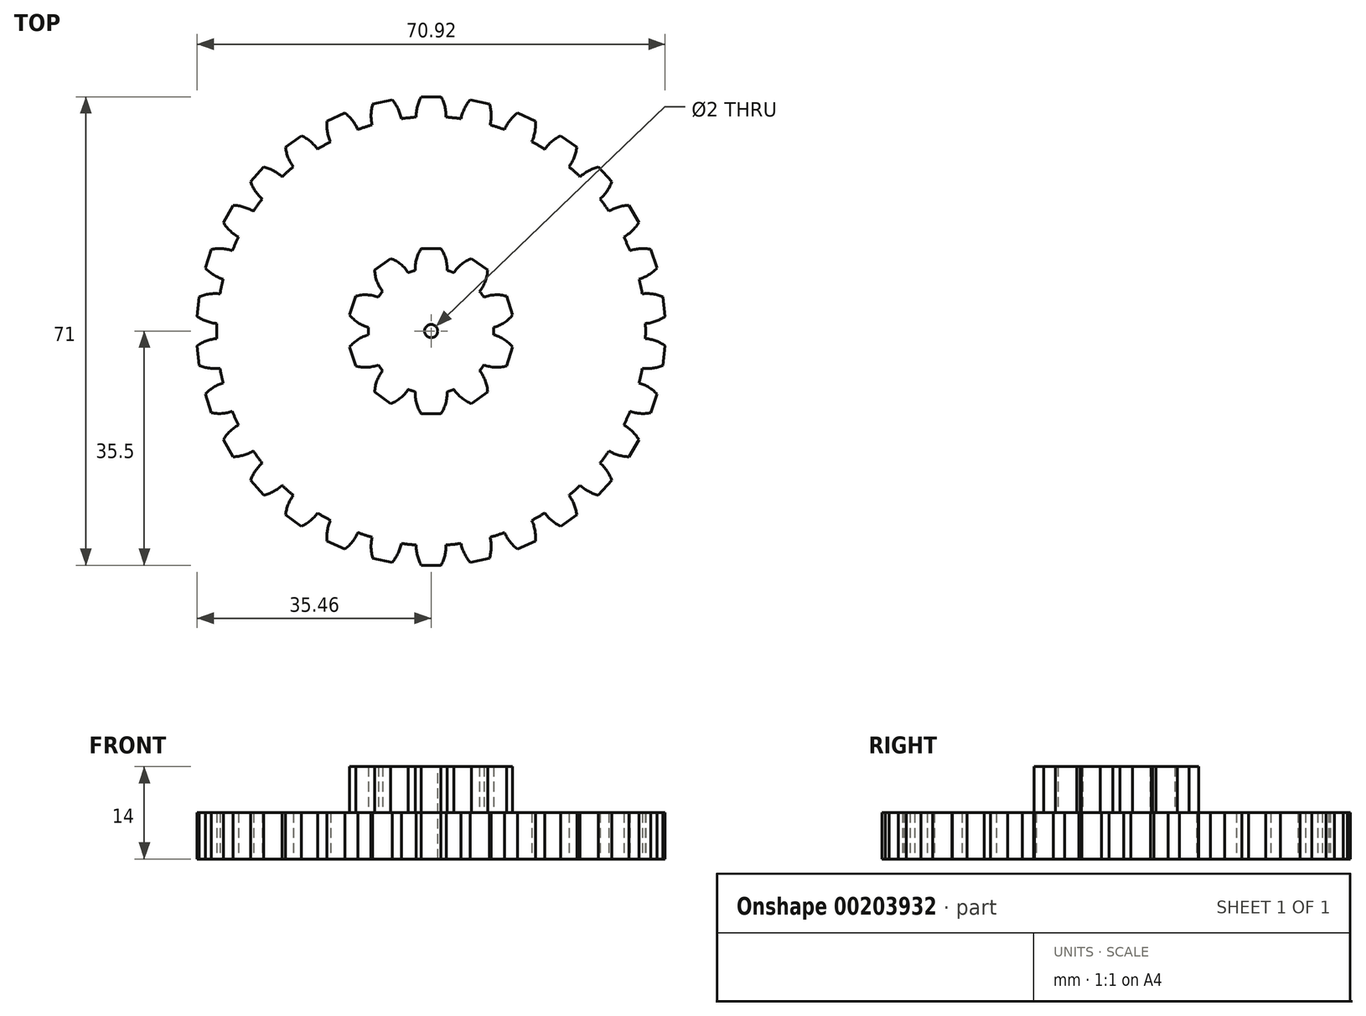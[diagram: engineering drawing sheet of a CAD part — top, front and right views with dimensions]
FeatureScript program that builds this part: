
annotation { "Feature Type Name" : "Feature", "Feature Type Description" : "" }
export const myFeature = defineFeature(function(context is Context, id is Id, definition is map)
    precondition{}
    {
        {
            var Q0;
            Q0=qCreatedBy(makeId("Top.planeOp"),FACE);
            var sketch = newSketch(context, id + "F0", { "sketchPlane" : qUnion([Q0])});
            skCircle(sketch, "E0", {"center": v(0, 0) * mm, "radius": 32.5 * mm});
            skLineSegment(sketch, "E1", {"start": v(0, 0) * mm, "end": v(0, 32.5) * mm, "construction": true});
            skLineSegment(sketch, "E2", {"start": v(0, 35.5) * mm, "end": v(-1.5, 35.5) * mm});
            skArc(sketch, "E3", {"start": v(-1.5, 35.5) * mm, "mid": v(-2.08, 34) * mm, "end": v(-2.26, 32.42) * mm});
            skLineSegment(sketch, "E4.MirrorCS", {"start": v(0, 35.5) * mm, "end": v(1.5, 35.5) * mm});
            skArc(sketch, "E5.MirrorCS", {"start": v(1.5, 35.5) * mm, "mid": v(2.08, 34) * mm, "end": v(2.26, 32.42) * mm});
            skArc(sketch, "E6.1.0", {"start": v(-8.85, 34.41) * mm, "mid": v(-9.1, 32.83) * mm, "end": v(-8.96, 31.24) * mm});
            skLineSegment(sketch, "E6.1.1", {"start": v(-7.38, 34.72) * mm, "end": v(-8.85, 34.41) * mm});
            skLineSegment(sketch, "E6.1.2", {"start": v(-7.38, 34.72) * mm, "end": v(-5.91, 35.04) * mm});
            skArc(sketch, "E6.1.3", {"start": v(-5.91, 35.04) * mm, "mid": v(-5.04, 33.7) * mm, "end": v(-4.53, 32.18) * mm});
            skArc(sketch, "E6.2.0", {"start": v(-15.8, 31.82) * mm, "mid": v(-15.73, 30.22) * mm, "end": v(-15.26, 28.7) * mm});
            skLineSegment(sketch, "E6.2.1", {"start": v(-14.44, 32.43) * mm, "end": v(-15.8, 31.82) * mm});
            skLineSegment(sketch, "E6.2.2", {"start": v(-14.44, 32.43) * mm, "end": v(-13.07, 33.04) * mm});
            skArc(sketch, "E6.2.3", {"start": v(-13.07, 33.04) * mm, "mid": v(-11.93, 31.92) * mm, "end": v(-11.12, 30.54) * mm});
            skArc(sketch, "E6.3.0", {"start": v(-22.08, 27.84) * mm, "mid": v(-21.67, 26.3) * mm, "end": v(-20.89, 24.9) * mm});
            skLineSegment(sketch, "E6.3.1", {"start": v(-20.87, 28.72) * mm, "end": v(-22.08, 27.84) * mm});
            skLineSegment(sketch, "E6.3.2", {"start": v(-20.87, 28.72) * mm, "end": v(-19.65, 29.6) * mm});
            skArc(sketch, "E6.3.3", {"start": v(-19.65, 29.6) * mm, "mid": v(-18.3, 28.74) * mm, "end": v(-17.22, 27.56) * mm});
            skArc(sketch, "E6.4.0", {"start": v(-27.39, 22.64) * mm, "mid": v(-26.67, 21.21) * mm, "end": v(-25.6, 20.01) * mm});
            skLineSegment(sketch, "E6.4.1", {"start": v(-26.38, 23.75) * mm, "end": v(-27.39, 22.64) * mm});
            skLineSegment(sketch, "E6.4.2", {"start": v(-26.38, 23.75) * mm, "end": v(-25.38, 24.87) * mm});
            skArc(sketch, "E6.4.3", {"start": v(-25.38, 24.87) * mm, "mid": v(-23.88, 24.3) * mm, "end": v(-22.58, 23.38) * mm});
            skArc(sketch, "E6.5.0", {"start": v(-31.5, 16.45) * mm, "mid": v(-30.5, 15.2) * mm, "end": v(-29.2, 14.25) * mm});
            skLineSegment(sketch, "E6.5.1", {"start": v(-30.74, 17.75) * mm, "end": v(-31.5, 16.45) * mm});
            skLineSegment(sketch, "E6.5.2", {"start": v(-30.74, 17.75) * mm, "end": v(-30, 19.05) * mm});
            skArc(sketch, "E6.5.3", {"start": v(-30, 19.05) * mm, "mid": v(-28.41, 18.8) * mm, "end": v(-26.95, 18.17) * mm});
            skArc(sketch, "E6.6.0", {"start": v(-34.23, 9.54) * mm, "mid": v(-32.99, 8.53) * mm, "end": v(-31.53, 7.86) * mm});
            skLineSegment(sketch, "E6.6.1", {"start": v(-33.76, 10.97) * mm, "end": v(-34.23, 9.54) * mm});
            skLineSegment(sketch, "E6.6.2", {"start": v(-33.76, 10.97) * mm, "end": v(-33.3, 12.4) * mm});
            skArc(sketch, "E6.6.3", {"start": v(-33.3, 12.4) * mm, "mid": v(-31.7, 12.49) * mm, "end": v(-30.13, 12.17) * mm});
            skArc(sketch, "E6.7.0", {"start": v(-35.46, 2.22) * mm, "mid": v(-34.04, 1.49) * mm, "end": v(-32.48, 1.14) * mm});
            skLineSegment(sketch, "E6.7.1", {"start": v(-35.3, 3.71) * mm, "end": v(-35.46, 2.22) * mm});
            skLineSegment(sketch, "E6.7.2", {"start": v(-35.3, 3.71) * mm, "end": v(-35.15, 5.2) * mm});
            skArc(sketch, "E6.7.3", {"start": v(-35.15, 5.2) * mm, "mid": v(-33.6, 5.62) * mm, "end": v(-32, 5.64) * mm});
            skArc(sketch, "E6.8.0", {"start": v(-35.15, -5.2) * mm, "mid": v(-33.6, -5.62) * mm, "end": v(-32, -5.64) * mm});
            skLineSegment(sketch, "E6.8.1", {"start": v(-35.3, -3.71) * mm, "end": v(-35.15, -5.2) * mm});
            skLineSegment(sketch, "E6.8.2", {"start": v(-35.3, -3.71) * mm, "end": v(-35.46, -2.22) * mm});
            skArc(sketch, "E6.8.3", {"start": v(-35.46, -2.22) * mm, "mid": v(-34.04, -1.49) * mm, "end": v(-32.48, -1.14) * mm});
            skArc(sketch, "E6.9.0", {"start": v(-33.3, -12.4) * mm, "mid": v(-31.7, -12.49) * mm, "end": v(-30.13, -12.17) * mm});
            skLineSegment(sketch, "E6.9.1", {"start": v(-33.76, -10.97) * mm, "end": v(-33.3, -12.4) * mm});
            skLineSegment(sketch, "E6.9.2", {"start": v(-33.76, -10.97) * mm, "end": v(-34.23, -9.54) * mm});
            skArc(sketch, "E6.9.3", {"start": v(-34.23, -9.54) * mm, "mid": v(-32.99, -8.53) * mm, "end": v(-31.53, -7.86) * mm});
            skArc(sketch, "E6.10.0", {"start": v(-30, -19.05) * mm, "mid": v(-28.41, -18.8) * mm, "end": v(-26.95, -18.17) * mm});
            skLineSegment(sketch, "E6.10.1", {"start": v(-30.74, -17.75) * mm, "end": v(-30, -19.05) * mm});
            skLineSegment(sketch, "E6.10.2", {"start": v(-30.74, -17.75) * mm, "end": v(-31.5, -16.45) * mm});
            skArc(sketch, "E6.10.3", {"start": v(-31.5, -16.45) * mm, "mid": v(-30.5, -15.2) * mm, "end": v(-29.2, -14.25) * mm});
            skArc(sketch, "E6.11.0", {"start": v(-25.38, -24.87) * mm, "mid": v(-23.88, -24.3) * mm, "end": v(-22.58, -23.38) * mm});
            skLineSegment(sketch, "E6.11.1", {"start": v(-26.38, -23.75) * mm, "end": v(-25.38, -24.87) * mm});
            skLineSegment(sketch, "E6.11.2", {"start": v(-26.38, -23.75) * mm, "end": v(-27.39, -22.64) * mm});
            skArc(sketch, "E6.11.3", {"start": v(-27.39, -22.64) * mm, "mid": v(-26.67, -21.21) * mm, "end": v(-25.6, -20.01) * mm});
            skArc(sketch, "E6.12.0", {"start": v(-19.65, -29.6) * mm, "mid": v(-18.3, -28.74) * mm, "end": v(-17.22, -27.56) * mm});
            skLineSegment(sketch, "E6.12.1", {"start": v(-20.87, -28.72) * mm, "end": v(-19.65, -29.6) * mm});
            skLineSegment(sketch, "E6.12.2", {"start": v(-20.87, -28.72) * mm, "end": v(-22.08, -27.84) * mm});
            skArc(sketch, "E6.12.3", {"start": v(-22.08, -27.84) * mm, "mid": v(-21.67, -26.3) * mm, "end": v(-20.89, -24.9) * mm});
            skArc(sketch, "E6.13.0", {"start": v(-13.07, -33.04) * mm, "mid": v(-11.93, -31.92) * mm, "end": v(-11.12, -30.54) * mm});
            skLineSegment(sketch, "E6.13.1", {"start": v(-14.44, -32.43) * mm, "end": v(-13.07, -33.04) * mm});
            skLineSegment(sketch, "E6.13.2", {"start": v(-14.44, -32.43) * mm, "end": v(-15.8, -31.82) * mm});
            skArc(sketch, "E6.13.3", {"start": v(-15.8, -31.82) * mm, "mid": v(-15.73, -30.22) * mm, "end": v(-15.26, -28.7) * mm});
            skArc(sketch, "E6.14.0", {"start": v(-5.91, -35.04) * mm, "mid": v(-5.04, -33.7) * mm, "end": v(-4.53, -32.18) * mm});
            skLineSegment(sketch, "E6.14.1", {"start": v(-7.38, -34.72) * mm, "end": v(-5.91, -35.04) * mm});
            skLineSegment(sketch, "E6.14.2", {"start": v(-7.38, -34.72) * mm, "end": v(-8.85, -34.41) * mm});
            skArc(sketch, "E6.14.3", {"start": v(-8.85, -34.41) * mm, "mid": v(-9.1, -32.83) * mm, "end": v(-8.96, -31.24) * mm});
            skArc(sketch, "E6.15.0", {"start": v(1.5, -35.5) * mm, "mid": v(2.08, -34) * mm, "end": v(2.26, -32.42) * mm});
            skLineSegment(sketch, "E6.15.1", {"start": v(0, -35.5) * mm, "end": v(1.5, -35.5) * mm});
            skLineSegment(sketch, "E6.15.2", {"start": v(0, -35.5) * mm, "end": v(-1.5, -35.5) * mm});
            skArc(sketch, "E6.15.3", {"start": v(-1.5, -35.5) * mm, "mid": v(-2.08, -34) * mm, "end": v(-2.26, -32.42) * mm});
            skArc(sketch, "E6.16.0", {"start": v(8.85, -34.41) * mm, "mid": v(9.1, -32.83) * mm, "end": v(8.96, -31.24) * mm});
            skLineSegment(sketch, "E6.16.1", {"start": v(7.38, -34.72) * mm, "end": v(8.85, -34.41) * mm});
            skLineSegment(sketch, "E6.16.2", {"start": v(7.38, -34.72) * mm, "end": v(5.91, -35.04) * mm});
            skArc(sketch, "E6.16.3", {"start": v(5.91, -35.04) * mm, "mid": v(5.04, -33.7) * mm, "end": v(4.53, -32.18) * mm});
            skArc(sketch, "E6.17.0", {"start": v(15.8, -31.82) * mm, "mid": v(15.73, -30.22) * mm, "end": v(15.26, -28.7) * mm});
            skLineSegment(sketch, "E6.17.1", {"start": v(14.44, -32.43) * mm, "end": v(15.8, -31.82) * mm});
            skLineSegment(sketch, "E6.17.2", {"start": v(14.44, -32.43) * mm, "end": v(13.07, -33.04) * mm});
            skArc(sketch, "E6.17.3", {"start": v(13.07, -33.04) * mm, "mid": v(11.93, -31.92) * mm, "end": v(11.12, -30.54) * mm});
            skArc(sketch, "E6.18.0", {"start": v(22.08, -27.84) * mm, "mid": v(21.67, -26.3) * mm, "end": v(20.89, -24.9) * mm});
            skLineSegment(sketch, "E6.18.1", {"start": v(20.87, -28.72) * mm, "end": v(22.08, -27.84) * mm});
            skLineSegment(sketch, "E6.18.2", {"start": v(20.87, -28.72) * mm, "end": v(19.65, -29.6) * mm});
            skArc(sketch, "E6.18.3", {"start": v(19.65, -29.6) * mm, "mid": v(18.3, -28.74) * mm, "end": v(17.22, -27.56) * mm});
            skArc(sketch, "E6.19.0", {"start": v(27.39, -22.64) * mm, "mid": v(26.67, -21.21) * mm, "end": v(25.6, -20.01) * mm});
            skLineSegment(sketch, "E6.19.1", {"start": v(26.38, -23.75) * mm, "end": v(27.39, -22.64) * mm});
            skLineSegment(sketch, "E6.19.2", {"start": v(26.38, -23.75) * mm, "end": v(25.38, -24.87) * mm});
            skArc(sketch, "E6.19.3", {"start": v(25.38, -24.87) * mm, "mid": v(23.88, -24.3) * mm, "end": v(22.58, -23.38) * mm});
            skArc(sketch, "E6.20.0", {"start": v(31.5, -16.45) * mm, "mid": v(30.5, -15.2) * mm, "end": v(29.2, -14.25) * mm});
            skLineSegment(sketch, "E6.20.1", {"start": v(30.74, -17.75) * mm, "end": v(31.5, -16.45) * mm});
            skLineSegment(sketch, "E6.20.2", {"start": v(30.74, -17.75) * mm, "end": v(30, -19.05) * mm});
            skArc(sketch, "E6.20.3", {"start": v(30, -19.05) * mm, "mid": v(28.41, -18.8) * mm, "end": v(26.95, -18.17) * mm});
            skArc(sketch, "E6.21.0", {"start": v(34.23, -9.54) * mm, "mid": v(32.99, -8.53) * mm, "end": v(31.53, -7.86) * mm});
            skLineSegment(sketch, "E6.21.1", {"start": v(33.76, -10.97) * mm, "end": v(34.23, -9.54) * mm});
            skLineSegment(sketch, "E6.21.2", {"start": v(33.76, -10.97) * mm, "end": v(33.3, -12.4) * mm});
            skArc(sketch, "E6.21.3", {"start": v(33.3, -12.4) * mm, "mid": v(31.7, -12.49) * mm, "end": v(30.13, -12.17) * mm});
            skArc(sketch, "E6.22.0", {"start": v(35.46, -2.22) * mm, "mid": v(34.04, -1.49) * mm, "end": v(32.48, -1.14) * mm});
            skLineSegment(sketch, "E6.22.1", {"start": v(35.3, -3.71) * mm, "end": v(35.46, -2.22) * mm});
            skLineSegment(sketch, "E6.22.2", {"start": v(35.3, -3.71) * mm, "end": v(35.15, -5.2) * mm});
            skArc(sketch, "E6.22.3", {"start": v(35.15, -5.2) * mm, "mid": v(33.6, -5.62) * mm, "end": v(32, -5.64) * mm});
            skArc(sketch, "E6.23.0", {"start": v(35.15, 5.2) * mm, "mid": v(33.6, 5.62) * mm, "end": v(32, 5.64) * mm});
            skLineSegment(sketch, "E6.23.1", {"start": v(35.3, 3.71) * mm, "end": v(35.15, 5.2) * mm});
            skLineSegment(sketch, "E6.23.2", {"start": v(35.3, 3.71) * mm, "end": v(35.46, 2.22) * mm});
            skArc(sketch, "E6.23.3", {"start": v(35.46, 2.22) * mm, "mid": v(34.04, 1.49) * mm, "end": v(32.48, 1.14) * mm});
            skArc(sketch, "E6.24.0", {"start": v(33.3, 12.4) * mm, "mid": v(31.7, 12.49) * mm, "end": v(30.13, 12.17) * mm});
            skLineSegment(sketch, "E6.24.1", {"start": v(33.76, 10.97) * mm, "end": v(33.3, 12.4) * mm});
            skLineSegment(sketch, "E6.24.2", {"start": v(33.76, 10.97) * mm, "end": v(34.23, 9.54) * mm});
            skArc(sketch, "E6.24.3", {"start": v(34.23, 9.54) * mm, "mid": v(32.99, 8.53) * mm, "end": v(31.53, 7.86) * mm});
            skArc(sketch, "E6.25.0", {"start": v(30, 19.05) * mm, "mid": v(28.41, 18.8) * mm, "end": v(26.95, 18.17) * mm});
            skLineSegment(sketch, "E6.25.1", {"start": v(30.74, 17.75) * mm, "end": v(30, 19.05) * mm});
            skLineSegment(sketch, "E6.25.2", {"start": v(30.74, 17.75) * mm, "end": v(31.5, 16.45) * mm});
            skArc(sketch, "E6.25.3", {"start": v(31.5, 16.45) * mm, "mid": v(30.5, 15.2) * mm, "end": v(29.2, 14.25) * mm});
            skArc(sketch, "E6.26.0", {"start": v(25.38, 24.87) * mm, "mid": v(23.88, 24.3) * mm, "end": v(22.58, 23.38) * mm});
            skLineSegment(sketch, "E6.26.1", {"start": v(26.38, 23.75) * mm, "end": v(25.38, 24.87) * mm});
            skLineSegment(sketch, "E6.26.2", {"start": v(26.38, 23.75) * mm, "end": v(27.39, 22.64) * mm});
            skArc(sketch, "E6.26.3", {"start": v(27.39, 22.64) * mm, "mid": v(26.67, 21.21) * mm, "end": v(25.6, 20.01) * mm});
            skArc(sketch, "E6.27.0", {"start": v(19.65, 29.6) * mm, "mid": v(18.3, 28.74) * mm, "end": v(17.22, 27.56) * mm});
            skLineSegment(sketch, "E6.27.1", {"start": v(20.87, 28.72) * mm, "end": v(19.65, 29.6) * mm});
            skLineSegment(sketch, "E6.27.2", {"start": v(20.87, 28.72) * mm, "end": v(22.08, 27.84) * mm});
            skArc(sketch, "E6.27.3", {"start": v(22.08, 27.84) * mm, "mid": v(21.67, 26.3) * mm, "end": v(20.89, 24.9) * mm});
            skArc(sketch, "E6.28.0", {"start": v(13.07, 33.04) * mm, "mid": v(11.93, 31.92) * mm, "end": v(11.12, 30.54) * mm});
            skLineSegment(sketch, "E6.28.1", {"start": v(14.44, 32.43) * mm, "end": v(13.07, 33.04) * mm});
            skLineSegment(sketch, "E6.28.2", {"start": v(14.44, 32.43) * mm, "end": v(15.8, 31.82) * mm});
            skArc(sketch, "E6.28.3", {"start": v(15.8, 31.82) * mm, "mid": v(15.73, 30.22) * mm, "end": v(15.26, 28.7) * mm});
            skArc(sketch, "E6.29.0", {"start": v(5.91, 35.04) * mm, "mid": v(5.04, 33.7) * mm, "end": v(4.53, 32.18) * mm});
            skLineSegment(sketch, "E6.29.1", {"start": v(7.38, 34.72) * mm, "end": v(5.91, 35.04) * mm});
            skLineSegment(sketch, "E6.29.2", {"start": v(7.38, 34.72) * mm, "end": v(8.85, 34.41) * mm});
            skArc(sketch, "E6.29.3", {"start": v(8.85, 34.41) * mm, "mid": v(9.1, 32.83) * mm, "end": v(8.96, 31.24) * mm});
            skSolve(sketch);
        }
        {
            var Q0;
            Q0=qSketchRegion(id+"F0",true);
            extrude(context, id + "F1", {"entities" : qUnion([Q0]), "depth" : 7 * mm});
        }
        {
            var Q0;
            Q0=makeQuery(id+"F1.opExtrude","CAP_FACE",FACE,{"disambiguationData":[OSD([sQuery(id+"F0.wireOp",EDGE,"E0"),sQuery(id+"F0.wireOp",EDGE,"E2"),sQuery(id+"F0.wireOp",EDGE,"E3"),sQuery(id+"F0.wireOp",EDGE,"E4.MirrorCS"),sQuery(id+"F0.wireOp",EDGE,"E5.MirrorCS"),sQuery(id+"F0.wireOp",EDGE,"E6.1.0"),sQuery(id+"F0.wireOp",EDGE,"E6.1.1"),sQuery(id+"F0.wireOp",EDGE,"E6.1.2"),sQuery(id+"F0.wireOp",EDGE,"E6.1.3"),sQuery(id+"F0.wireOp",EDGE,"E6.2.0"),sQuery(id+"F0.wireOp",EDGE,"E6.2.1"),sQuery(id+"F0.wireOp",EDGE,"E6.2.2"),sQuery(id+"F0.wireOp",EDGE,"E6.2.3"),sQuery(id+"F0.wireOp",EDGE,"E6.3.0"),sQuery(id+"F0.wireOp",EDGE,"E6.3.1"),sQuery(id+"F0.wireOp",EDGE,"E6.3.2"),sQuery(id+"F0.wireOp",EDGE,"E6.3.3"),sQuery(id+"F0.wireOp",EDGE,"E6.4.0"),sQuery(id+"F0.wireOp",EDGE,"E6.4.1"),sQuery(id+"F0.wireOp",EDGE,"E6.4.2"),sQuery(id+"F0.wireOp",EDGE,"E6.4.3"),sQuery(id+"F0.wireOp",EDGE,"E6.5.0"),sQuery(id+"F0.wireOp",EDGE,"E6.5.1"),sQuery(id+"F0.wireOp",EDGE,"E6.5.2"),sQuery(id+"F0.wireOp",EDGE,"E6.5.3"),sQuery(id+"F0.wireOp",EDGE,"E6.6.0"),sQuery(id+"F0.wireOp",EDGE,"E6.6.1"),sQuery(id+"F0.wireOp",EDGE,"E6.6.2"),sQuery(id+"F0.wireOp",EDGE,"E6.6.3"),sQuery(id+"F0.wireOp",EDGE,"E6.7.0"),sQuery(id+"F0.wireOp",EDGE,"E6.7.1"),sQuery(id+"F0.wireOp",EDGE,"E6.7.2"),sQuery(id+"F0.wireOp",EDGE,"E6.7.3"),sQuery(id+"F0.wireOp",EDGE,"E6.8.0"),sQuery(id+"F0.wireOp",EDGE,"E6.8.1"),sQuery(id+"F0.wireOp",EDGE,"E6.8.2"),sQuery(id+"F0.wireOp",EDGE,"E6.8.3"),sQuery(id+"F0.wireOp",EDGE,"E6.9.0"),sQuery(id+"F0.wireOp",EDGE,"E6.9.1"),sQuery(id+"F0.wireOp",EDGE,"E6.9.2"),sQuery(id+"F0.wireOp",EDGE,"E6.9.3"),sQuery(id+"F0.wireOp",EDGE,"E6.10.0"),sQuery(id+"F0.wireOp",EDGE,"E6.10.1"),sQuery(id+"F0.wireOp",EDGE,"E6.10.2"),sQuery(id+"F0.wireOp",EDGE,"E6.10.3"),sQuery(id+"F0.wireOp",EDGE,"E6.11.0"),sQuery(id+"F0.wireOp",EDGE,"E6.11.1"),sQuery(id+"F0.wireOp",EDGE,"E6.11.2"),sQuery(id+"F0.wireOp",EDGE,"E6.11.3"),sQuery(id+"F0.wireOp",EDGE,"E6.12.0"),sQuery(id+"F0.wireOp",EDGE,"E6.12.1"),sQuery(id+"F0.wireOp",EDGE,"E6.12.2"),sQuery(id+"F0.wireOp",EDGE,"E6.12.3"),sQuery(id+"F0.wireOp",EDGE,"E6.13.0"),sQuery(id+"F0.wireOp",EDGE,"E6.13.1"),sQuery(id+"F0.wireOp",EDGE,"E6.13.2"),sQuery(id+"F0.wireOp",EDGE,"E6.13.3"),sQuery(id+"F0.wireOp",EDGE,"E6.14.0"),sQuery(id+"F0.wireOp",EDGE,"E6.14.1"),sQuery(id+"F0.wireOp",EDGE,"E6.14.2"),sQuery(id+"F0.wireOp",EDGE,"E6.14.3"),sQuery(id+"F0.wireOp",EDGE,"E6.15.0"),sQuery(id+"F0.wireOp",EDGE,"E6.15.1"),sQuery(id+"F0.wireOp",EDGE,"E6.15.2"),sQuery(id+"F0.wireOp",EDGE,"E6.15.3"),sQuery(id+"F0.wireOp",EDGE,"E6.16.0"),sQuery(id+"F0.wireOp",EDGE,"E6.16.1"),sQuery(id+"F0.wireOp",EDGE,"E6.16.2"),sQuery(id+"F0.wireOp",EDGE,"E6.16.3"),sQuery(id+"F0.wireOp",EDGE,"E6.17.0"),sQuery(id+"F0.wireOp",EDGE,"E6.17.1"),sQuery(id+"F0.wireOp",EDGE,"E6.17.2"),sQuery(id+"F0.wireOp",EDGE,"E6.17.3"),sQuery(id+"F0.wireOp",EDGE,"E6.18.0"),sQuery(id+"F0.wireOp",EDGE,"E6.18.1"),sQuery(id+"F0.wireOp",EDGE,"E6.18.2"),sQuery(id+"F0.wireOp",EDGE,"E6.18.3"),sQuery(id+"F0.wireOp",EDGE,"E6.19.0"),sQuery(id+"F0.wireOp",EDGE,"E6.19.1"),sQuery(id+"F0.wireOp",EDGE,"E6.19.2"),sQuery(id+"F0.wireOp",EDGE,"E6.19.3"),sQuery(id+"F0.wireOp",EDGE,"E6.20.0"),sQuery(id+"F0.wireOp",EDGE,"E6.20.1"),sQuery(id+"F0.wireOp",EDGE,"E6.20.2"),sQuery(id+"F0.wireOp",EDGE,"E6.20.3"),sQuery(id+"F0.wireOp",EDGE,"E6.21.0"),sQuery(id+"F0.wireOp",EDGE,"E6.21.1"),sQuery(id+"F0.wireOp",EDGE,"E6.21.2"),sQuery(id+"F0.wireOp",EDGE,"E6.21.3"),sQuery(id+"F0.wireOp",EDGE,"E6.22.0"),sQuery(id+"F0.wireOp",EDGE,"E6.22.1"),sQuery(id+"F0.wireOp",EDGE,"E6.22.2"),sQuery(id+"F0.wireOp",EDGE,"E6.22.3"),sQuery(id+"F0.wireOp",EDGE,"E6.23.0"),sQuery(id+"F0.wireOp",EDGE,"E6.23.1"),sQuery(id+"F0.wireOp",EDGE,"E6.23.2"),sQuery(id+"F0.wireOp",EDGE,"E6.23.3"),sQuery(id+"F0.wireOp",EDGE,"E6.24.0"),sQuery(id+"F0.wireOp",EDGE,"E6.24.1"),sQuery(id+"F0.wireOp",EDGE,"E6.24.2"),sQuery(id+"F0.wireOp",EDGE,"E6.24.3"),sQuery(id+"F0.wireOp",EDGE,"E6.25.0"),sQuery(id+"F0.wireOp",EDGE,"E6.25.1"),sQuery(id+"F0.wireOp",EDGE,"E6.25.2"),sQuery(id+"F0.wireOp",EDGE,"E6.25.3"),sQuery(id+"F0.wireOp",EDGE,"E6.26.0"),sQuery(id+"F0.wireOp",EDGE,"E6.26.1"),sQuery(id+"F0.wireOp",EDGE,"E6.26.2"),sQuery(id+"F0.wireOp",EDGE,"E6.26.3"),sQuery(id+"F0.wireOp",EDGE,"E6.27.0"),sQuery(id+"F0.wireOp",EDGE,"E6.27.1"),sQuery(id+"F0.wireOp",EDGE,"E6.27.2"),sQuery(id+"F0.wireOp",EDGE,"E6.27.3"),sQuery(id+"F0.wireOp",EDGE,"E6.28.0"),sQuery(id+"F0.wireOp",EDGE,"E6.28.1"),sQuery(id+"F0.wireOp",EDGE,"E6.28.2"),sQuery(id+"F0.wireOp",EDGE,"E6.28.3"),sQuery(id+"F0.wireOp",EDGE,"E6.29.0"),sQuery(id+"F0.wireOp",EDGE,"E6.29.1"),sQuery(id+"F0.wireOp",EDGE,"E6.29.2"),sQuery(id+"F0.wireOp",EDGE,"E6.29.3")])],"isStart":false});
            var sketch = newSketch(context, id + "F2", { "sketchPlane" : qUnion([Q0])});
            skCircle(sketch, "E7", {"center": v(0, 0) * mm, "radius": 9.5 * mm});
            skLineSegment(sketch, "E8", {"start": v(0, 0) * mm, "end": v(0, 9.5) * mm, "construction": true});
            skLineSegment(sketch, "E9", {"start": v(0, 12.5) * mm, "end": v(-1.5, 12.5) * mm});
            skArc(sketch, "E10", {"start": v(-1.5, 12.5) * mm, "mid": v(-2.22, 10.92) * mm, "end": v(-2.4, 9.2) * mm});
            skLineSegment(sketch, "E11.MirrorCS", {"start": v(0, 12.5) * mm, "end": v(1.5, 12.5) * mm});
            skArc(sketch, "E12.MirrorCS", {"start": v(1.5, 12.5) * mm, "mid": v(2.22, 10.92) * mm, "end": v(2.4, 9.2) * mm});
            skArc(sketch, "E13.1.0", {"start": v(-8.56, 9.23) * mm, "mid": v(-8.21, 7.53) * mm, "end": v(-7.34, 6.03) * mm});
            skLineSegment(sketch, "E13.1.1", {"start": v(-7.35, 10.11) * mm, "end": v(-8.56, 9.23) * mm});
            skLineSegment(sketch, "E13.1.2", {"start": v(-7.35, 10.11) * mm, "end": v(-6.13, 11) * mm});
            skArc(sketch, "E13.1.3", {"start": v(-6.13, 11) * mm, "mid": v(-4.62, 10.14) * mm, "end": v(-3.46, 8.85) * mm});
            skArc(sketch, "E13.2.0", {"start": v(-12.35, 2.44) * mm, "mid": v(-11.07, 1.26) * mm, "end": v(-9.48, 0.56) * mm});
            skLineSegment(sketch, "E13.2.1", {"start": v(-11.89, 3.86) * mm, "end": v(-12.35, 2.44) * mm});
            skLineSegment(sketch, "E13.2.2", {"start": v(-11.89, 3.86) * mm, "end": v(-11.42, 5.29) * mm});
            skArc(sketch, "E13.2.3", {"start": v(-11.42, 5.29) * mm, "mid": v(-9.7, 5.48) * mm, "end": v(-8, 5.12) * mm});
            skArc(sketch, "E13.3.0", {"start": v(-11.42, -5.29) * mm, "mid": v(-9.7, -5.48) * mm, "end": v(-8, -5.12) * mm});
            skLineSegment(sketch, "E13.3.1", {"start": v(-11.89, -3.86) * mm, "end": v(-11.42, -5.29) * mm});
            skLineSegment(sketch, "E13.3.2", {"start": v(-11.89, -3.86) * mm, "end": v(-12.35, -2.44) * mm});
            skArc(sketch, "E13.3.3", {"start": v(-12.35, -2.44) * mm, "mid": v(-11.07, -1.26) * mm, "end": v(-9.48, -0.56) * mm});
            skArc(sketch, "E13.4.0", {"start": v(-6.13, -11) * mm, "mid": v(-4.62, -10.14) * mm, "end": v(-3.46, -8.85) * mm});
            skLineSegment(sketch, "E13.4.1", {"start": v(-7.35, -10.11) * mm, "end": v(-6.13, -11) * mm});
            skLineSegment(sketch, "E13.4.2", {"start": v(-7.35, -10.11) * mm, "end": v(-8.56, -9.23) * mm});
            skArc(sketch, "E13.4.3", {"start": v(-8.56, -9.23) * mm, "mid": v(-8.21, -7.53) * mm, "end": v(-7.34, -6.03) * mm});
            skArc(sketch, "E13.5.0", {"start": v(1.5, -12.5) * mm, "mid": v(2.22, -10.92) * mm, "end": v(2.4, -9.2) * mm});
            skLineSegment(sketch, "E13.5.1", {"start": v(0, -12.5) * mm, "end": v(1.5, -12.5) * mm});
            skLineSegment(sketch, "E13.5.2", {"start": v(0, -12.5) * mm, "end": v(-1.5, -12.5) * mm});
            skArc(sketch, "E13.5.3", {"start": v(-1.5, -12.5) * mm, "mid": v(-2.22, -10.92) * mm, "end": v(-2.4, -9.2) * mm});
            skArc(sketch, "E13.6.0", {"start": v(8.56, -9.23) * mm, "mid": v(8.21, -7.53) * mm, "end": v(7.34, -6.03) * mm});
            skLineSegment(sketch, "E13.6.1", {"start": v(7.35, -10.11) * mm, "end": v(8.56, -9.23) * mm});
            skLineSegment(sketch, "E13.6.2", {"start": v(7.35, -10.11) * mm, "end": v(6.13, -11) * mm});
            skArc(sketch, "E13.6.3", {"start": v(6.13, -11) * mm, "mid": v(4.62, -10.14) * mm, "end": v(3.46, -8.85) * mm});
            skArc(sketch, "E13.7.0", {"start": v(12.35, -2.44) * mm, "mid": v(11.07, -1.26) * mm, "end": v(9.48, -0.56) * mm});
            skLineSegment(sketch, "E13.7.1", {"start": v(11.89, -3.86) * mm, "end": v(12.35, -2.44) * mm});
            skLineSegment(sketch, "E13.7.2", {"start": v(11.89, -3.86) * mm, "end": v(11.42, -5.29) * mm});
            skArc(sketch, "E13.7.3", {"start": v(11.42, -5.29) * mm, "mid": v(9.7, -5.48) * mm, "end": v(8, -5.12) * mm});
            skArc(sketch, "E13.8.0", {"start": v(11.42, 5.29) * mm, "mid": v(9.7, 5.48) * mm, "end": v(8, 5.12) * mm});
            skLineSegment(sketch, "E13.8.1", {"start": v(11.89, 3.86) * mm, "end": v(11.42, 5.29) * mm});
            skLineSegment(sketch, "E13.8.2", {"start": v(11.89, 3.86) * mm, "end": v(12.35, 2.44) * mm});
            skArc(sketch, "E13.8.3", {"start": v(12.35, 2.44) * mm, "mid": v(11.07, 1.26) * mm, "end": v(9.48, 0.56) * mm});
            skArc(sketch, "E13.9.0", {"start": v(6.13, 11) * mm, "mid": v(4.62, 10.14) * mm, "end": v(3.46, 8.85) * mm});
            skLineSegment(sketch, "E13.9.1", {"start": v(7.35, 10.11) * mm, "end": v(6.13, 11) * mm});
            skLineSegment(sketch, "E13.9.2", {"start": v(7.35, 10.11) * mm, "end": v(8.56, 9.23) * mm});
            skArc(sketch, "E13.9.3", {"start": v(8.56, 9.23) * mm, "mid": v(8.21, 7.53) * mm, "end": v(7.34, 6.03) * mm});
            skSolve(sketch);
        }
        {
            var Q0;
            Q0=qSketchRegion(id+"F2",true);
            extrude(context, id + "F3", {"entities" : qUnion([Q0]), "operationType" : NewBodyOperationType.ADD, "depth" : 7 * mm});
        }
        {
            var Q0;
            Q0=makeQuery(id+"F3.opExtrude","CAP_FACE",FACE,{"disambiguationData":[OSD([sQuery(id+"F2.wireOp",EDGE,"E7"),sQuery(id+"F2.wireOp",EDGE,"E9"),sQuery(id+"F2.wireOp",EDGE,"E10"),sQuery(id+"F2.wireOp",EDGE,"E11.MirrorCS"),sQuery(id+"F2.wireOp",EDGE,"E12.MirrorCS"),sQuery(id+"F2.wireOp",EDGE,"E13.1.0"),sQuery(id+"F2.wireOp",EDGE,"E13.1.1"),sQuery(id+"F2.wireOp",EDGE,"E13.1.2"),sQuery(id+"F2.wireOp",EDGE,"E13.1.3"),sQuery(id+"F2.wireOp",EDGE,"E13.2.0"),sQuery(id+"F2.wireOp",EDGE,"E13.2.1"),sQuery(id+"F2.wireOp",EDGE,"E13.2.2"),sQuery(id+"F2.wireOp",EDGE,"E13.2.3"),sQuery(id+"F2.wireOp",EDGE,"E13.3.0"),sQuery(id+"F2.wireOp",EDGE,"E13.3.1"),sQuery(id+"F2.wireOp",EDGE,"E13.3.2"),sQuery(id+"F2.wireOp",EDGE,"E13.3.3"),sQuery(id+"F2.wireOp",EDGE,"E13.4.0"),sQuery(id+"F2.wireOp",EDGE,"E13.4.1"),sQuery(id+"F2.wireOp",EDGE,"E13.4.2"),sQuery(id+"F2.wireOp",EDGE,"E13.4.3"),sQuery(id+"F2.wireOp",EDGE,"E13.5.0"),sQuery(id+"F2.wireOp",EDGE,"E13.5.1"),sQuery(id+"F2.wireOp",EDGE,"E13.5.2"),sQuery(id+"F2.wireOp",EDGE,"E13.5.3"),sQuery(id+"F2.wireOp",EDGE,"E13.6.0"),sQuery(id+"F2.wireOp",EDGE,"E13.6.1"),sQuery(id+"F2.wireOp",EDGE,"E13.6.2"),sQuery(id+"F2.wireOp",EDGE,"E13.6.3"),sQuery(id+"F2.wireOp",EDGE,"E13.7.0"),sQuery(id+"F2.wireOp",EDGE,"E13.7.1"),sQuery(id+"F2.wireOp",EDGE,"E13.7.2"),sQuery(id+"F2.wireOp",EDGE,"E13.7.3"),sQuery(id+"F2.wireOp",EDGE,"E13.8.0"),sQuery(id+"F2.wireOp",EDGE,"E13.8.1"),sQuery(id+"F2.wireOp",EDGE,"E13.8.2"),sQuery(id+"F2.wireOp",EDGE,"E13.8.3"),sQuery(id+"F2.wireOp",EDGE,"E13.9.0"),sQuery(id+"F2.wireOp",EDGE,"E13.9.1"),sQuery(id+"F2.wireOp",EDGE,"E13.9.2"),sQuery(id+"F2.wireOp",EDGE,"E13.9.3")])],"isStart":false});
            var sketch = newSketch(context, id + "F4", { "sketchPlane" : qUnion([Q0])});
            skCircle(sketch, "E14", {"center": v(0, 0) * mm, "radius": 1 * mm});
            skSolve(sketch);
        }
        {
            var Q0;
            Q0=qSketchRegion(id+"F4",true);
            extrude(context, id + "F5", {"entities" : qUnion([Q0]), "operationType" : NewBodyOperationType.REMOVE, "oppositeDirection" : true, "depth" : 25 * mm});
        }
    });
